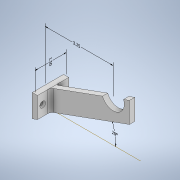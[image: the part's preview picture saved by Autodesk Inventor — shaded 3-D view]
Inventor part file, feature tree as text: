
AUTODESK INVENTOR PART (.ipt)
format: ipt  version: 2021.1 (Build 251245010, 245A)  size: 375,296 bytes
history: native  units: in
note: dims shown in document units (in); Inventor stores cm internally (conversion verified against a paired STEP export)
features: sketch x5, other x4, extrude x4, hole x1, fillet x1
ambient origin geometry x8: Origin, YZ Plane, XZ Plane, XY Plane, X Axis, Y Axis, Z Axis, Center Point
bodies: Solid2 (feature_tree)
feature tree (15):
  other  "Annotations"
  extrude  "Extrusion3"  Depth=0.25in
  extrude  "Extrusion4"  Depth=0.1374in
  sketch  "Sketch7"  dims[d26=1.075in d29=0.25in]
  extrude  "Extrusion5"  Depth=0.25in
  hole  "Hole3"  [1 undecoded]
  extrude  "Extrusion6"  TaperAngle=0.0deg  [1 undecoded]
  fillet  "Fillet1"  Radius=0.25in
  sketch  "Sketch5"  dims[d21=1.0in d22=0.25in]
  sketch  "Sketch6"  dims[d23=1.5in d24=0.0in d25=0.1374in]
  sketch  "Sketch8"  dims[d30=3.25in d31=0.25in]
  sketch  "Sketch9"  dims[d32=0.0in d33=0.0in d34=0.25in d35=0.25in d47=1.5in d48=0.0in d49=0.15in d50=0.75in d51=0.279in d52=0.25in d53=0.5635in d54=1.0in d55=0.8108in d63=0.05in d64=0.0in d65=0.125in d56=0.2085in d57=0.331in d58=1.5in d59=2.3174in d60=0.1374in d62=3.25in]
  other  "Linear Dimension 1"
  other  "Angular Dimension 1"
  other  "Linear Dimension 3"
note: 2 required parameter values undecoded (feature->parameter linkage not recoverable at this tier; creation-order binding heuristic only, values carry confidence <= 0.55)
